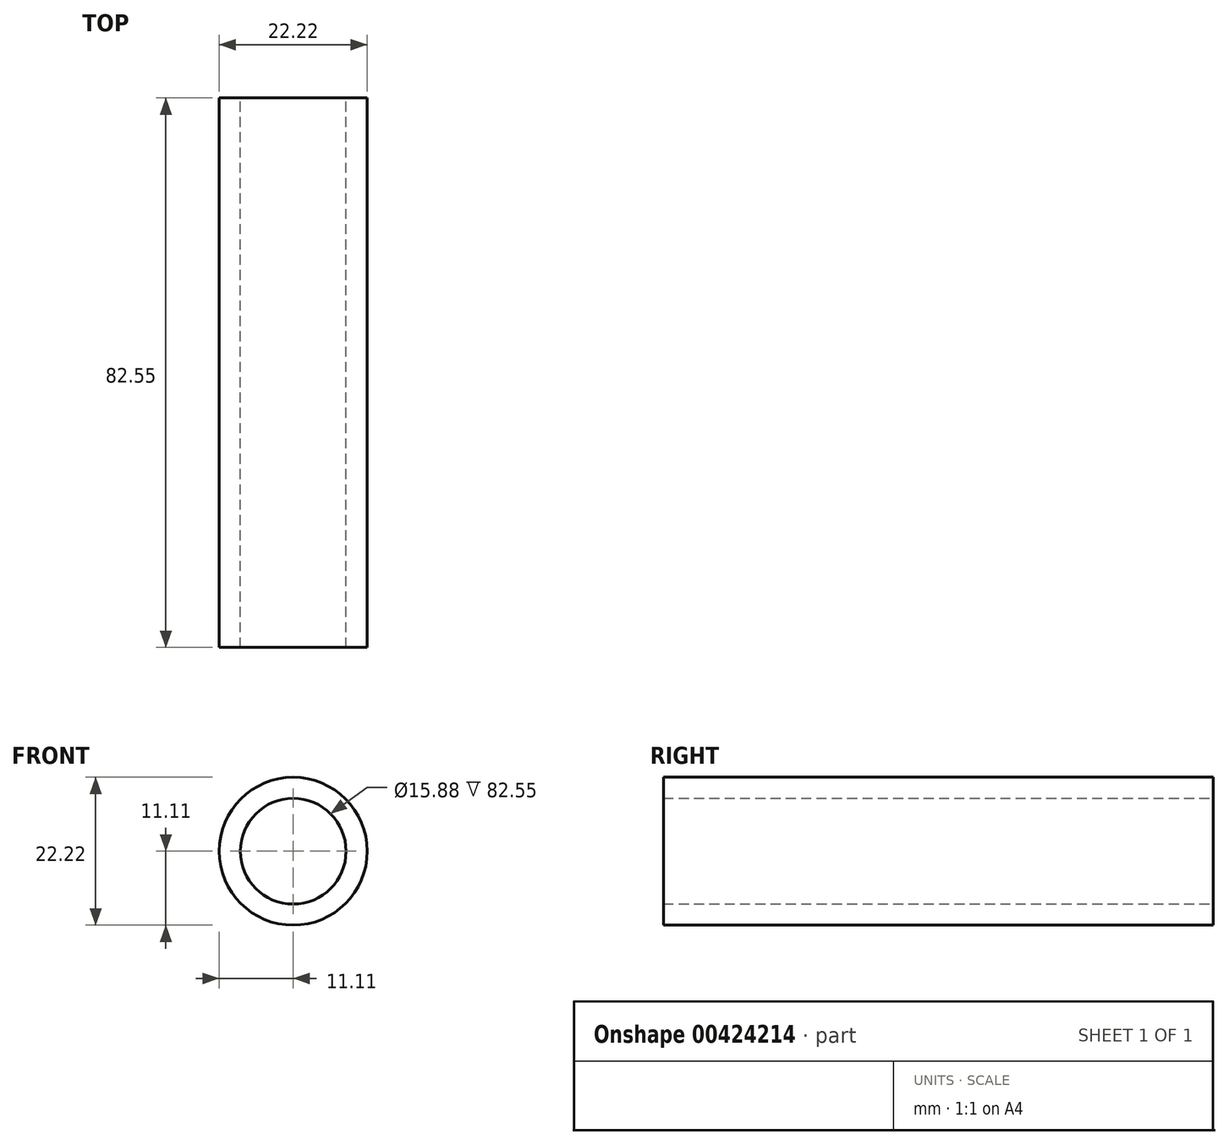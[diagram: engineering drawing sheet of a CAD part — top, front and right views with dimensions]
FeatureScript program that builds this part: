
annotation { "Feature Type Name" : "Feature", "Feature Type Description" : "" }
export const myFeature = defineFeature(function(context is Context, id is Id, definition is map)
    precondition{}
    {
        {
            var Q0;
            Q0=qCreatedBy(makeId("Front.planeOp"),FACE);
            var sketch = newSketch(context, id + "F0", { "sketchPlane" : qUnion([Q0])});
            skCircle(sketch, "E0", {"center": v(0, 0) * mm, "radius": 11.11 * mm});
            skCircle(sketch, "E1", {"center": v(0, 0) * mm, "radius": 7.94 * mm});
            skSolve(sketch);
        }
        {
            var Q0;
            Q0 = qSketchRegion(id + "F0", true);
            extrude(context, id + "F1", {"entities" : qUnion([Q0]), "depth" : 82.55 * mm});
        }
    });
